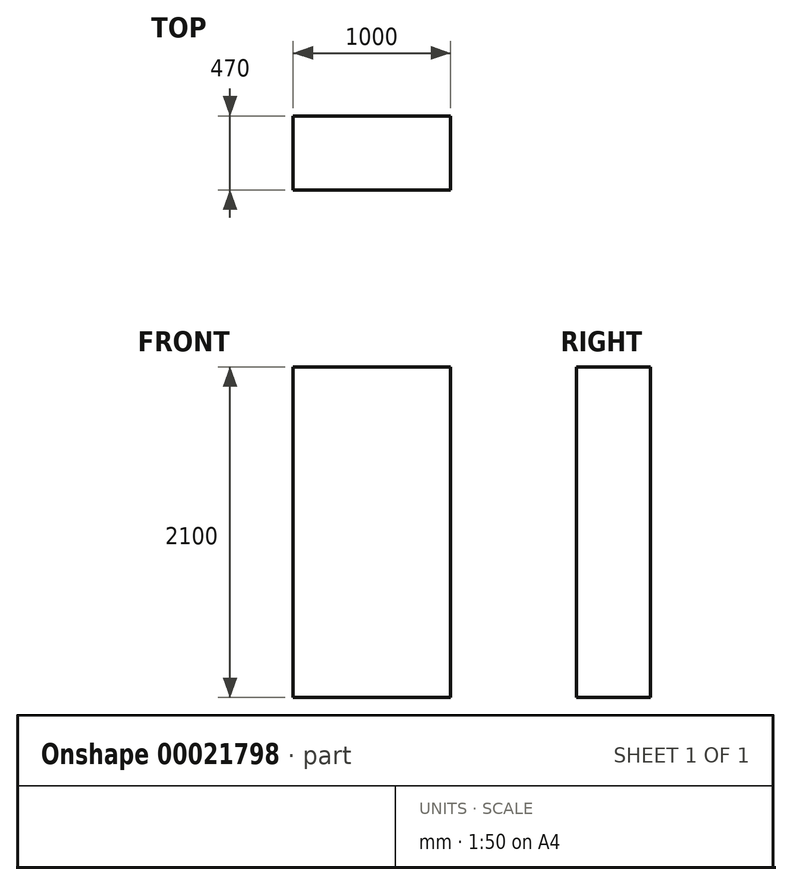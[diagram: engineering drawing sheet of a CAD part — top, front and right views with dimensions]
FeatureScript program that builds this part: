
annotation { "Feature Type Name" : "Feature", "Feature Type Description" : "" }
export const myFeature = defineFeature(function(context is Context, id is Id, definition is map)
    precondition{}
    {
        {
            var Q0;
            Q0=qCreatedBy(makeId("Top.planeOp"),FACE);
            var sketch = newSketch(context, id + "F0", { "sketchPlane" : qUnion([Q0])});
            skLineSegment(sketch, "E0.bottom", {"start": v(0, 0) * mm, "end": v(1000, 0) * mm});
            skLineSegment(sketch, "E0.top", {"start": v(0, 470) * mm, "end": v(1000, 470) * mm});
            skLineSegment(sketch, "E0.left", {"start": v(0, 0) * mm, "end": v(0, 470) * mm});
            skLineSegment(sketch, "E0.right", {"start": v(1000, 0) * mm, "end": v(1000, 470) * mm});
            skSolve(sketch);
        }
        {
            var Q0;
            Q0=makeQuery(id+"F0.imprint","IMPRINT",FACE,{"disambiguationData":[TD([[makeQuery(id+"F0.imprint","IMPRINT",EDGE,{"derivedFrom":sQuery(id+"F0.wireOp",EDGE,"E0.bottom")}),1.0]])]});
            extrude(context, id + "F1", {"entities" : qUnion([Q0]), "depth" : 2100 * mm});
        }
    });
